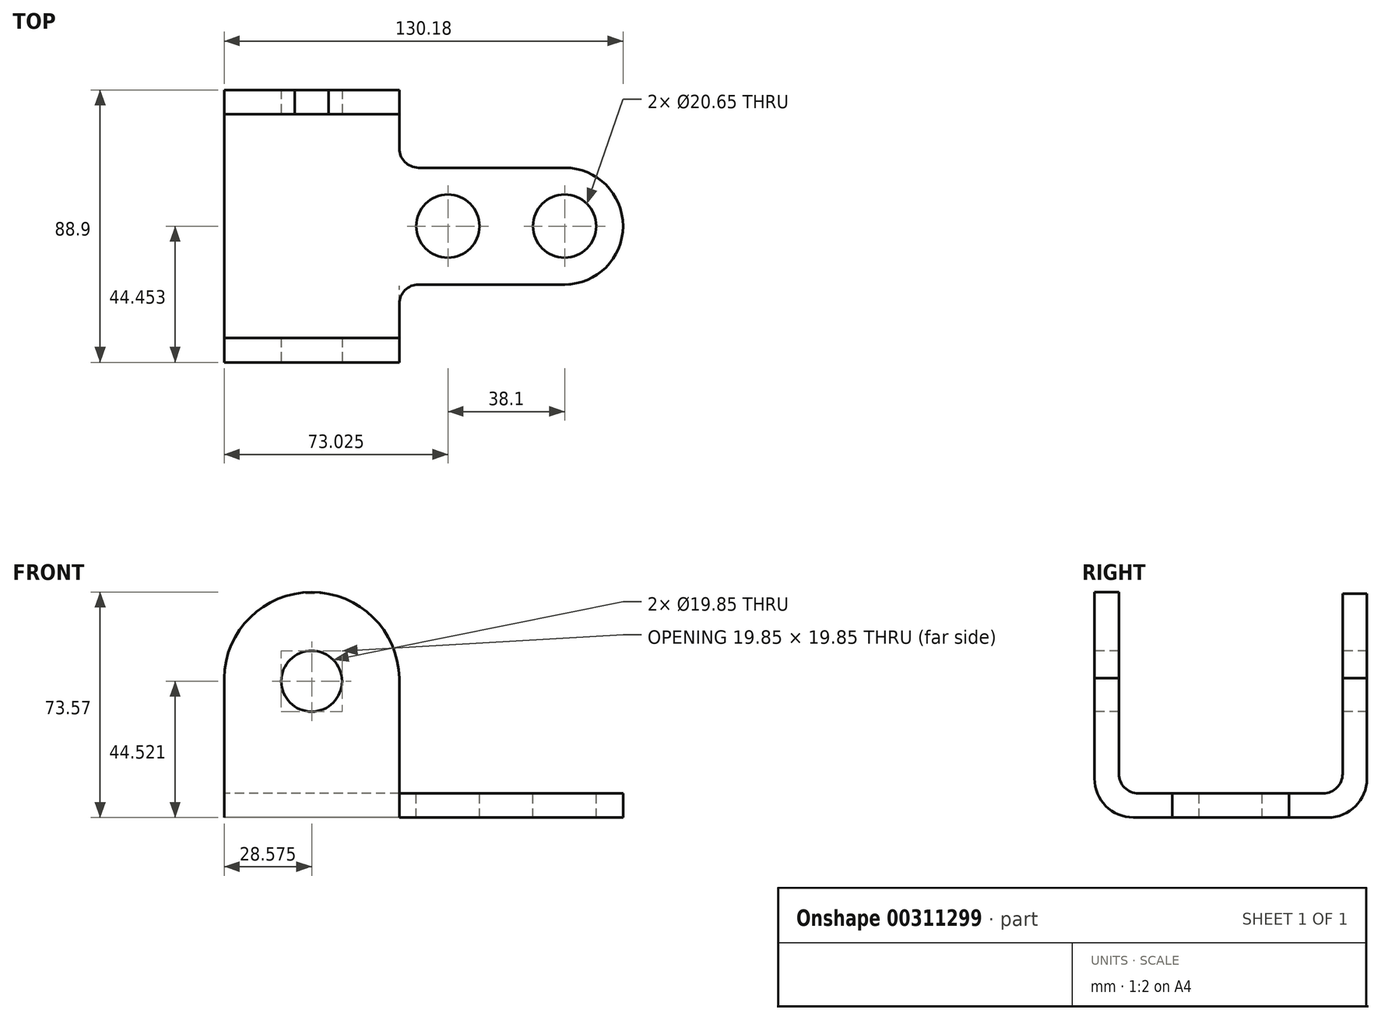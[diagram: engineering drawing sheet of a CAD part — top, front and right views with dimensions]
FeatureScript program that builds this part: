
annotation { "Feature Type Name" : "Feature", "Feature Type Description" : "" }
export const myFeature = defineFeature(function(context is Context, id is Id, definition is map)
    precondition{}
    {
        {
            var Q0;
            Q0=qCreatedBy(makeId("Right.planeOp"),FACE);
            var sketch = newSketch(context, id + "F0", { "sketchPlane" : qUnion([Q0])});
            skLineSegment(sketch, "E0", {"start": v(42.86, 65.09) * mm, "end": v(42.86, 4.76) * mm});
            skLineSegment(sketch, "E1", {"start": v(-46.04, 4.81) * mm, "end": v(-46.04, 65.63) * mm});
            skLineSegment(sketch, "E2", {"start": v(-46.04, 65.63) * mm, "end": v(-38.1, 65.63) * mm});
            skLineSegment(sketch, "E3", {"start": v(-38.1, 65.63) * mm, "end": v(-38.1, 6.35) * mm});
            skLineSegment(sketch, "E4", {"start": v(34.93, 6.35) * mm, "end": v(34.93, 65.09) * mm});
            skLineSegment(sketch, "E5", {"start": v(34.93, 65.09) * mm, "end": v(42.86, 65.09) * mm});
            skPoint(sketch, "E6.visualSharp", {"position": v(42.86, -7.94) * mm});
            skPoint(sketch, "E7.visualSharp", {"position": v(34.93, 0) * mm});
            skPoint(sketch, "E8.visualSharp", {"position": v(-46.04, -7.94) * mm});
            skPoint(sketch, "E9.visualSharp", {"position": v(-38.1, 0) * mm});
            skPoint(sketch, "E10", {"position": v(0, 0) * mm});
            skPoint(sketch, "E11.visualSharp", {"position": v(-46.04, -7.75) * mm});
            skLineSegment(sketch, "E12", {"start": v(28.58, 0) * mm, "end": v(17.46, 0) * mm});
            skLineSegment(sketch, "E13", {"start": v(42.86, -7.94) * mm, "end": v(34.93, -7.94) * mm});
            skLineSegment(sketch, "E14", {"start": v(30.16, -7.94) * mm, "end": v(17.46, -7.94) * mm});
            skLineSegment(sketch, "E15", {"start": v(-46.04, -7.87) * mm, "end": v(-38.1, -7.87) * mm});
            skLineSegment(sketch, "E16", {"start": v(-33.39, -7.89) * mm, "end": v(-20.64, -7.94) * mm});
            skLineSegment(sketch, "E17", {"start": v(-31.75, 0) * mm, "end": v(-20.64, 0) * mm});
            skLineSegment(sketch, "E18", {"start": v(-20.64, 0) * mm, "end": v(17.46, 0) * mm});
            skLineSegment(sketch, "E19", {"start": v(17.46, -7.94) * mm, "end": v(-20.64, -7.94) * mm});
            skLineSegment(sketch, "E20", {"start": v(17.46, 0) * mm, "end": v(17.46, -7.94) * mm});
            skLineSegment(sketch, "E21", {"start": v(-20.64, 0) * mm, "end": v(-20.64, -7.94) * mm});
            skPoint(sketch, "E22.newPointB", {"position": v(-38.1, -7.87) * mm});
            skArc(sketch, "E22.filletArc", {"start": v(-46.04, 4.81) * mm, "mid": v(-42.34, -4.15) * mm, "end": v(-33.39, -7.89) * mm});
            skArc(sketch, "E23.filletArc", {"start": v(-38.1, 6.35) * mm, "mid": v(-36.24, 1.86) * mm, "end": v(-31.75, 0) * mm});
            skArc(sketch, "E24.filletArc", {"start": v(28.58, 0) * mm, "mid": v(33.07, 1.86) * mm, "end": v(34.93, 6.35) * mm});
            skPoint(sketch, "E25.newPointB", {"position": v(34.93, -7.94) * mm});
            skArc(sketch, "E25.filletArc", {"start": v(30.16, -7.94) * mm, "mid": v(39.14, -4.22) * mm, "end": v(42.86, 4.76) * mm});
            skSolve(sketch);
        }
        {
            var Q0;
            Q0=makeQuery(id+"F0.imprint","IMPRINT",FACE,{"disambiguationData":[TD([[makeQuery(id+"F0.imprint","IMPRINT",EDGE,{"derivedFrom":sQuery(id+"F0.wireOp",EDGE,"E18")}),-1.0]])]});
            extrude(context, id + "F1", {"entities" : qUnion([Q0]), "depth" : 133.35 * mm});
        }
        {
            var Q0;
            Q0=makeQuery(id+"F0.imprint","IMPRINT",FACE,{"disambiguationData":[TD([[makeQuery(id+"F0.imprint","IMPRINT",EDGE,{"derivedFrom":sQuery(id+"F0.wireOp",EDGE,"E1")}),-1.0]])]});
            var Q1;
            {var subQ1=sQuery(id+"F0.wireOp",EDGE,"E4");Q1=makeQuery(id+"F0.imprint","IMPRINT",FACE,{"disambiguationData":[TD([[makeQuery(id+"F0.imprint","IMPRINT",EDGE,{"derivedFrom":subQ1}),-1.0]])]});}
            extrude(context, id + "F2", {"entities" : qUnion([Q0, Q1]), "operationType" : NewBodyOperationType.ADD, "depth" : 57.15 * mm});
        }
        {
            var Q0;
            Q0=makeQuery(id+"F2.opExtrude","SWEPT_FACE",FACE,{"disambiguationData":[OSD([sQuery(id+"F0.wireOp",EDGE,"E1")])]});
            var sketch = newSketch(context, id + "F3", { "sketchPlane" : qUnion([Q0])});
            skCircle(sketch, "E26", {"center": v(28.58, 36.58) * mm, "radius": 9.92 * mm});
            skPoint(sketch, "E26.centerSnap0", {"position": v(28.58, 65.63) * mm});
            skArc(sketch, "E27", {"start": v(57.15, 36.58) * mm, "mid": v(28.58, 65.63) * mm, "end": v(0, 36.58) * mm});
            skLineSegment(sketch, "E28", {"start": v(0, 36.58) * mm, "end": v(0, 65.63) * mm});
            skLineSegment(sketch, "E29", {"start": v(0, 65.63) * mm, "end": v(28.58, 65.63) * mm});
            skLineSegment(sketch, "E30", {"start": v(57.15, 65.63) * mm, "end": v(57.15, 36.58) * mm});
            skSolve(sketch);
        }
        {
            var Q0;
            {var subQ0=sQuery(id+"F3.wireOp",EDGE,"E29");Q0=makeQuery(id+"F3.imprint","IMPRINT",FACE,{"disambiguationData":[TD([[makeQuery(id+"F3.imprint","IMPRINT",EDGE,{"derivedFrom":subQ0}),1.0]])]});}
            var Q1;
            {var subQ0=sQuery(id+"F3.wireOp",EDGE,"E27");var subQ3=sQuery(id+"F3.wireOp",EDGE,"E30");var subQ4=makeQuery(id+"F3.imprint","INTERSECT",VERTEX,{"derivedFrom":[subQ0,subQ3]});Q1=makeQuery(id+"F3.imprint","IMPRINT",FACE,{"disambiguationData":[TD([[makeQuery(id+"F3.imprint","IMPRINT",EDGE,{"disambiguationData":[TD([[subQ4,-1.0]])],"derivedFrom":subQ3}),1.0]])]});}
            var Q2;
            Q2=makeQuery(id+"F3.imprint","IMPRINT",FACE,{"disambiguationData":[TD([[makeQuery(id+"F3.imprint","IMPRINT",EDGE,{"derivedFrom":sQuery(id+"F3.wireOp",EDGE,"E26")}),1.0]])]});
            extrude(context, id + "F4", {"entities" : qUnion([Q0, Q1, Q2]), "operationType" : NewBodyOperationType.REMOVE, "endBound" : BoundingType.THROUGH_ALL, "oppositeDirection" : true, "depth" : 25.4 * mm});
        }
        {
            var Q0;
            Q0=makeQuery(id+"F2.boolean.opBoolean","MERGE",FACE,{"derivedFrom":[makeQuery(id+"F1.opExtrude","SWEPT_FACE",FACE,{"disambiguationData":[OSD([sQuery(id+"F0.wireOp",EDGE,"E18")])]}),makeQuery(id+"F2.opExtrude","SWEPT_FACE",FACE,{"disambiguationData":[OSD([sQuery(id+"F0.wireOp",EDGE,"E12")])]}),makeQuery(id+"F2.opExtrude","SWEPT_FACE",FACE,{"disambiguationData":[OSD([sQuery(id+"F0.wireOp",EDGE,"E17")])]})]});
            var sketch = newSketch(context, id + "F5", { "sketchPlane" : qUnion([Q0])});
            skLineSegment(sketch, "E31", {"start": v(0, 34.93) * mm, "end": v(57.15, 34.93) * mm});
            skLineSegment(sketch, "E32", {"start": v(57.15, 34.93) * mm, "end": v(57.15, 23.81) * mm});
            skLineSegment(sketch, "E33", {"start": v(57.15, -26.99) * mm, "end": v(57.15, -38.1) * mm});
            skLineSegment(sketch, "E34", {"start": v(57.15, -38.1) * mm, "end": v(0, -38.1) * mm});
            skLineSegment(sketch, "E35", {"start": v(0, -38.1) * mm, "end": v(0, 34.93) * mm});
            skPoint(sketch, "E36.visualSharp", {"position": v(57.15, 17.46) * mm});
            skArc(sketch, "E36.filletArc", {"start": v(57.15, 23.81) * mm, "mid": v(59, 19.34) * mm, "end": v(63.46, 17.46) * mm});
            skPoint(sketch, "E37.visualSharp", {"position": v(57.15, -20.64) * mm});
            skArc(sketch, "E37.filletArc", {"start": v(63.5, -20.64) * mm, "mid": v(59.01, -22.5) * mm, "end": v(57.15, -26.99) * mm});
            skPoint(sketch, "E38.visualSharp", {"position": v(133.35, 17.46) * mm});
            skPoint(sketch, "E39.visualSharp", {"position": v(133.35, -20.64) * mm});
            skCircle(sketch, "E40", {"center": v(73.03, -1.59) * mm, "radius": 10.33 * mm});
            skCircle(sketch, "E41", {"center": v(111.13, -1.59) * mm, "radius": 10.33 * mm});
            skLineSegment(sketch, "E42", {"start": v(57.15, 23.81) * mm, "end": v(57.15, 17.46) * mm});
            skLineSegment(sketch, "E43", {"start": v(63.46, 17.46) * mm, "end": v(133.35, 17.46) * mm});
            skLineSegment(sketch, "E44", {"start": v(133.35, -20.64) * mm, "end": v(133.35, 17.46) * mm});
            skLineSegment(sketch, "E45", {"start": v(133.35, -20.64) * mm, "end": v(63.5, -20.64) * mm});
            skLineSegment(sketch, "E46", {"start": v(57.15, -20.64) * mm, "end": v(57.15, -26.99) * mm});
            skArc(sketch, "E47", {"start": v(111.13, -20.64) * mm, "mid": v(130.18, -1.59) * mm, "end": v(111.13, 17.46) * mm});
            skSolve(sketch);
        }
        {
            var Q0;
            {var subQ0=sQuery(id+"F5.wireOp",EDGE,"E36.filletArc");Q0=makeQuery(id+"F5.imprint","IMPRINT",FACE,{"disambiguationData":[TD([[makeQuery(id+"F5.imprint","IMPRINT",EDGE,{"derivedFrom":subQ0}),-1.0]])]});}
            var Q1;
            {var subQ0=sQuery(id+"F5.wireOp",EDGE,"E37.filletArc");Q1=makeQuery(id+"F5.imprint","IMPRINT",FACE,{"disambiguationData":[TD([[makeQuery(id+"F5.imprint","IMPRINT",EDGE,{"derivedFrom":subQ0}),-1.0]])]});}
            extrude(context, id + "F6", {"entities" : qUnion([Q0, Q1]), "operationType" : NewBodyOperationType.ADD, "oppositeDirection" : true, "depth" : 7.94 * mm});
        }
        {
            var Q0;
            {var subQ0=sQuery(id+"F5.wireOp",EDGE,"E36.filletArc");Q0=makeQuery(id+"F5.imprint","IMPRINT",FACE,{"disambiguationData":[TD([[makeQuery(id+"F5.imprint","IMPRINT",EDGE,{"derivedFrom":subQ0}),-1.0]])]});}
            var Q1;
            {var subQ0=sQuery(id+"F5.wireOp",EDGE,"E46");Q1=makeQuery(id+"F5.imprint","IMPRINT",FACE,{"disambiguationData":[TD([[makeQuery(id+"F5.imprint","IMPRINT",EDGE,{"derivedFrom":subQ0}),-1.0]])]});}
            extrude(context, id + "F7", {"entities" : qUnion([Q0, Q1]), "operationType" : NewBodyOperationType.ADD, "oppositeDirection" : true, "depth" : 7.94 * mm});
        }
        {
            var Q0;
            {var subQ0=sQuery(id+"F5.wireOp",EDGE,"E44");Q0=makeQuery(id+"F5.imprint","IMPRINT",FACE,{"disambiguationData":[TD([[makeQuery(id+"F5.imprint","IMPRINT",EDGE,{"derivedFrom":subQ0}),1.0]])]});}
            extrude(context, id + "F8", {"entities" : qUnion([Q0]), "operationType" : NewBodyOperationType.REMOVE, "endBound" : BoundingType.THROUGH_ALL, "oppositeDirection" : true, "depth" : 25.4 * mm});
        }
        {
            var Q0;
            Q0=makeQuery(id+"F5.imprint","IMPRINT",FACE,{"disambiguationData":[TD([[makeQuery(id+"F5.imprint","IMPRINT",EDGE,{"derivedFrom":sQuery(id+"F5.wireOp",EDGE,"E40")}),1.0]])]});
            var Q1;
            Q1=makeQuery(id+"F5.imprint","IMPRINT",FACE,{"disambiguationData":[TD([[makeQuery(id+"F5.imprint","IMPRINT",EDGE,{"derivedFrom":sQuery(id+"F5.wireOp",EDGE,"E41")}),1.0]])]});
            extrude(context, id + "F9", {"entities" : qUnion([Q0, Q1]), "operationType" : NewBodyOperationType.REMOVE, "endBound" : BoundingType.THROUGH_ALL, "oppositeDirection" : true, "depth" : 25.4 * mm});
        }
    });
